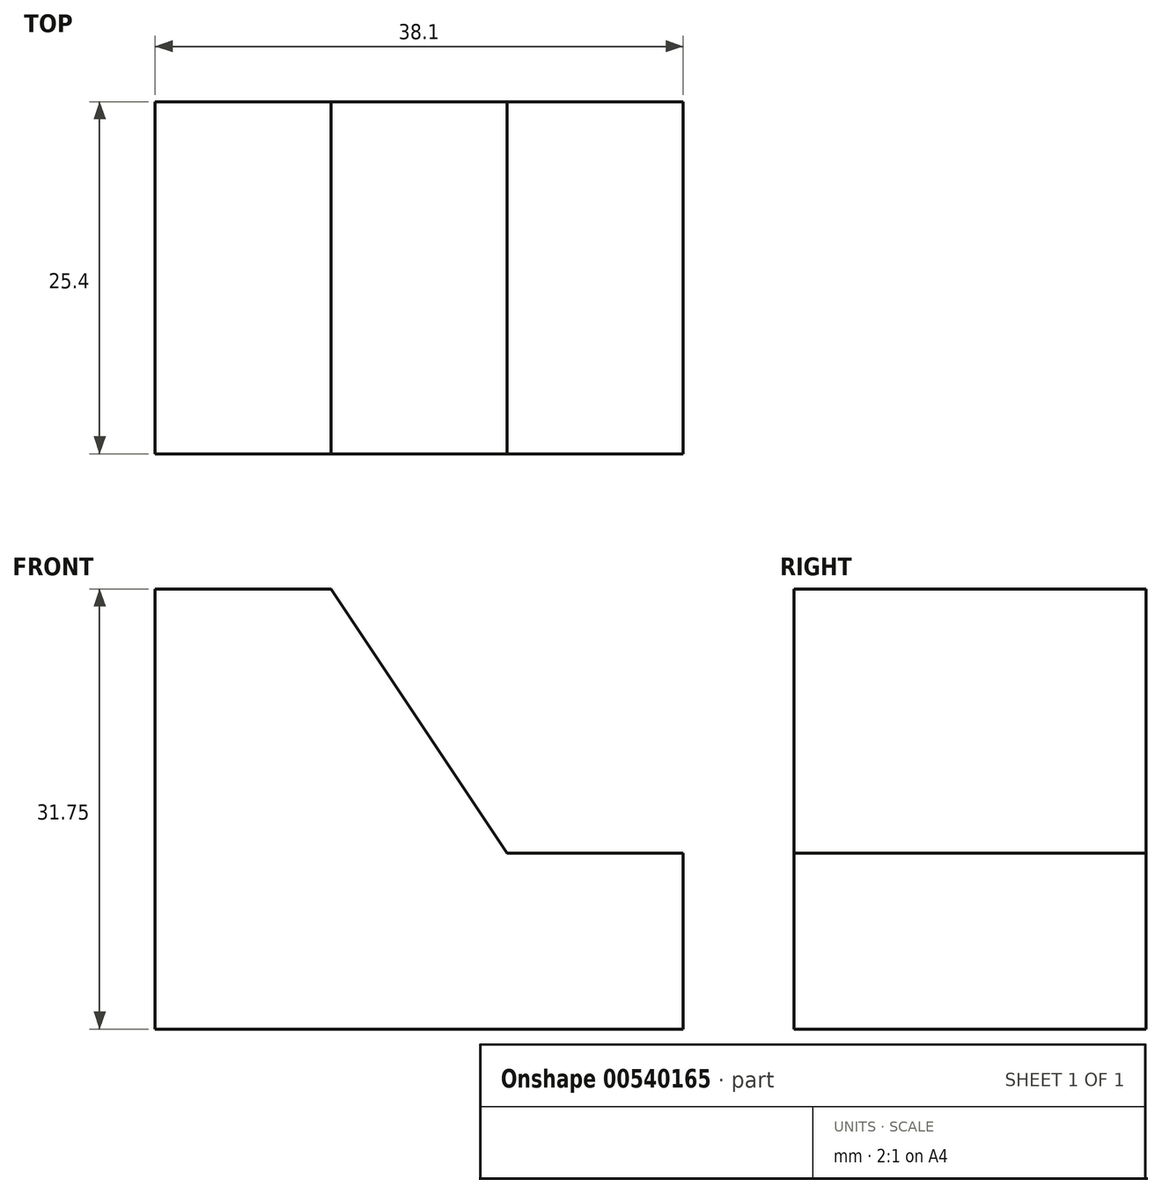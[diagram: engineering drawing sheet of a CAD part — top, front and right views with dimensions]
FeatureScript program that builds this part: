
annotation { "Feature Type Name" : "Feature", "Feature Type Description" : "" }
export const myFeature = defineFeature(function(context is Context, id is Id, definition is map)
    precondition{}
    {
        {
            var Q0;
            Q0=qCreatedBy(makeId("Front.planeOp"),FACE);
            var sketch = newSketch(context, id + "F0", { "sketchPlane" : qUnion([Q0])});
            skLineSegment(sketch, "E0", {"start": v(0, 0) * mm, "end": v(-38.1, 0) * mm});
            skLineSegment(sketch, "E1", {"start": v(-38.1, 0) * mm, "end": v(-38.1, 31.75) * mm});
            skLineSegment(sketch, "E2", {"start": v(-38.1, 31.75) * mm, "end": v(-25.4, 31.75) * mm});
            skLineSegment(sketch, "E3", {"start": v(0, 0) * mm, "end": v(0, 12.7) * mm});
            skLineSegment(sketch, "E4", {"start": v(0, 12.7) * mm, "end": v(-12.7, 12.7) * mm});
            skLineSegment(sketch, "E5", {"start": v(-12.7, 12.7) * mm, "end": v(-25.4, 31.75) * mm});
            skSolve(sketch);
        }
        {
            var Q0;
            Q0 = qSketchRegion(id + "F0", true);
            extrude(context, id + "F1", {"entities" : qUnion([Q0]), "oppositeDirection" : true, "depth" : 25.4 * mm, "offsetDistance" : 25.4 * mm});
        }
    });
